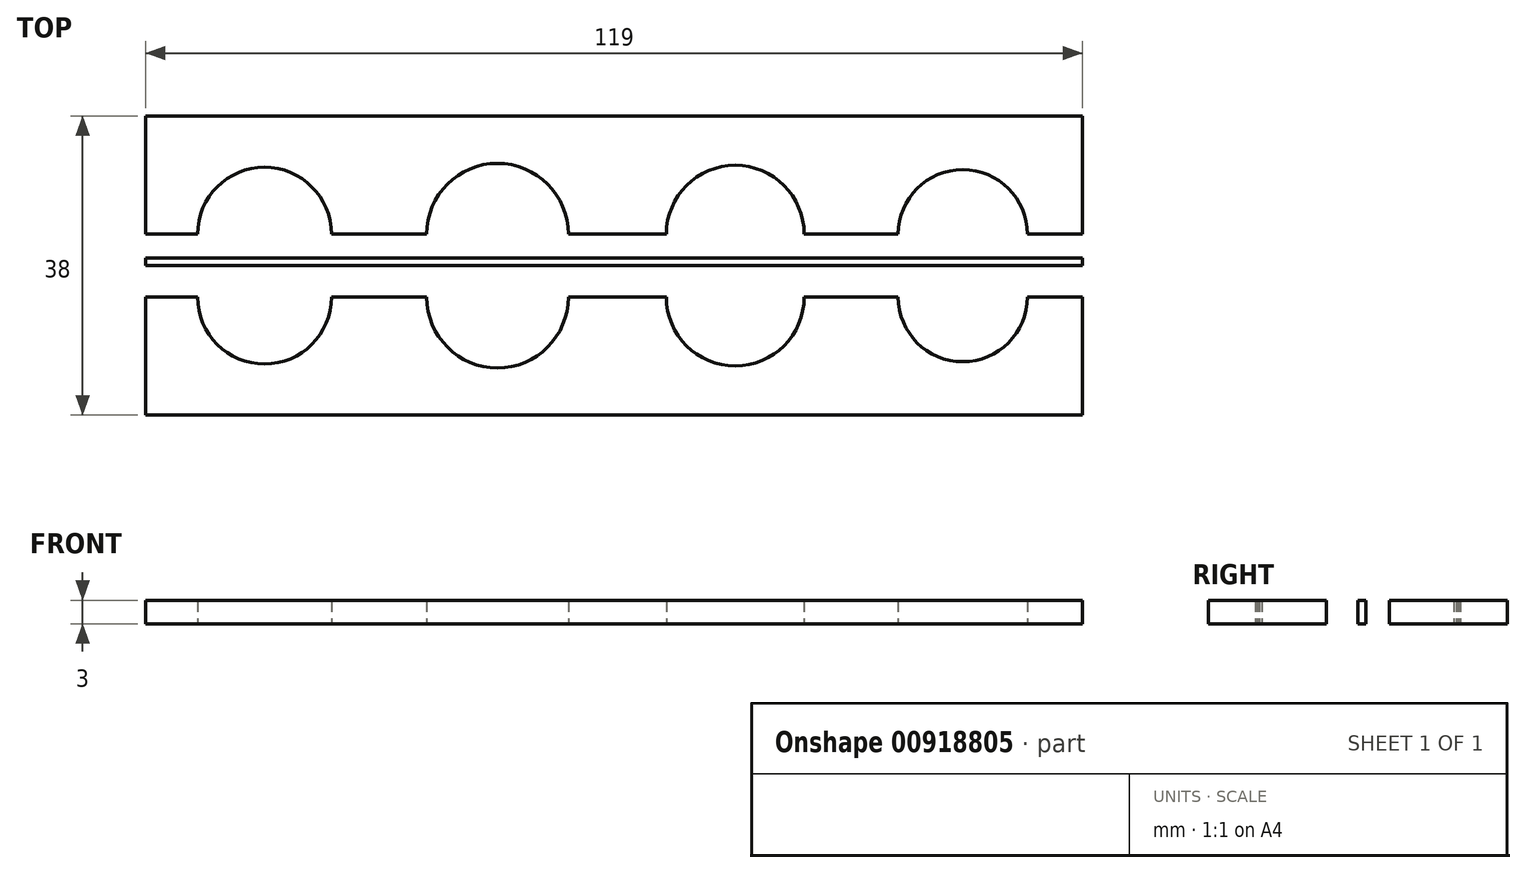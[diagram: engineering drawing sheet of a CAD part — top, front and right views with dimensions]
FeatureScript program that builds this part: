
annotation { "Feature Type Name" : "Feature", "Feature Type Description" : "" }
export const myFeature = defineFeature(function(context is Context, id is Id, definition is map)
    precondition{}
    {
        {
            var Q0;
            Q0=qCreatedBy(makeId("Top.planeOp"),FACE);
            var sketch = newSketch(context, id + "F0", { "sketchPlane" : qUnion([Q0])});
            skLineSegment(sketch, "E0.top", {"start": v(59.5, 15) * mm, "end": v(-59.5, 15) * mm});
            skLineSegment(sketch, "E0.left", {"start": v(59.5, 0) * mm, "end": v(59.5, 15) * mm});
            skLineSegment(sketch, "E0.right", {"start": v(-59.5, 0) * mm, "end": v(-59.5, 15) * mm});
            skPoint(sketch, "E0.middle", {"position": v(0, 0) * mm});
            skLineSegment(sketch, "E1", {"start": v(-59.5, 0) * mm, "end": v(-57.9, 0) * mm});
            skLineSegment(sketch, "E2", {"start": v(-57.9, 0) * mm, "end": v(-44.4, 0) * mm});
            skLineSegment(sketch, "E3", {"start": v(-44.4, 0) * mm, "end": v(-30.9, 0) * mm});
            skLineSegment(sketch, "E4", {"start": v(-30.9, 0) * mm, "end": v(-29.3, 0) * mm});
            skLineSegment(sketch, "E5", {"start": v(-29.3, 0) * mm, "end": v(-14.8, 0) * mm});
            skLineSegment(sketch, "E6", {"start": v(-14.8, 0) * mm, "end": v(-0.3, 0) * mm});
            skLineSegment(sketch, "E7", {"start": v(-0.3, 0) * mm, "end": v(1.3, 0) * mm});
            skLineSegment(sketch, "E8", {"start": v(1.3, 0) * mm, "end": v(15.4, 0) * mm});
            skLineSegment(sketch, "E9", {"start": v(15.4, 0) * mm, "end": v(29.5, 0) * mm});
            skLineSegment(sketch, "E10", {"start": v(29.5, 0) * mm, "end": v(31.1, 0) * mm});
            skLineSegment(sketch, "E11", {"start": v(31.1, 0) * mm, "end": v(44.3, 0) * mm});
            skLineSegment(sketch, "E12", {"start": v(44.3, 0) * mm, "end": v(57.5, 0) * mm});
            skLineSegment(sketch, "E13", {"start": v(57.5, 0) * mm, "end": v(59.5, 0) * mm});
            skArc(sketch, "E14", {"start": v(-35.9, 0) * mm, "mid": v(-44.4, 8.5) * mm, "end": v(-52.9, 0) * mm});
            skArc(sketch, "E15", {"start": v(-5.8, 0) * mm, "mid": v(-14.8, 9) * mm, "end": v(-23.8, 0) * mm});
            skArc(sketch, "E16", {"start": v(24.15, 0) * mm, "mid": v(15.4, 8.75) * mm, "end": v(6.65, 0) * mm});
            skArc(sketch, "E17", {"start": v(52.5, 0) * mm, "mid": v(44.3, 8.2) * mm, "end": v(36.1, 0) * mm});
            skPoint(sketch, "E0.bottom.end.orphan", {"position": v(-59.5, -15) * mm});
            skPoint(sketch, "E0.bottom.start.orphan", {"position": v(59.5, -15) * mm});
            skLineSegment(sketch, "E18", {"start": v(59.5, 0) * mm, "end": v(59.5, -3) * mm});
            skLineSegment(sketch, "E19", {"start": v(59.5, -3) * mm, "end": v(-57.9, -3) * mm});
            skLineSegment(sketch, "E20", {"start": v(-57.9, -3) * mm, "end": v(-59.5, -3) * mm});
            skLineSegment(sketch, "E21", {"start": v(-59.5, -3) * mm, "end": v(-59.5, 0) * mm});
            skLineSegment(sketch, "E22", {"start": v(-59.5, -3) * mm, "end": v(-59.5, -4) * mm});
            skLineSegment(sketch, "E23", {"start": v(-59.5, -4) * mm, "end": v(59.5, -4) * mm});
            skLineSegment(sketch, "E24", {"start": v(59.5, -4) * mm, "end": v(59.5, -3) * mm});
            skSolve(sketch);
        }
        {
            var Q0;
            Q0=makeQuery(id+"F0.imprint","IMPRINT",FACE,{"disambiguationData":[TD([[makeQuery(id+"F0.imprint","IMPRINT",EDGE,{"derivedFrom":sQuery(id+"F0.wireOp",EDGE,"E0.top")}),1.0]])]});
            var Q1;
            Q1=makeQuery(id+"F0.imprint","IMPRINT",FACE,{"disambiguationData":[TD([[makeQuery(id+"F0.imprint","IMPRINT",EDGE,{"derivedFrom":sQuery(id+"F0.wireOp",EDGE,"E19")}),1.0]])]});
            extrude(context, id + "F1", {"entities" : qUnion([Q0, Q1]), "depth" : 3 * mm, "offsetDistance" : 25 * mm});
        }
        {
            var Q0;
            Q0=makeQuery(id+"F1.opExtrude","SWEPT_BODY",BODY,{"disambiguationData":[OSD([sQuery(id+"F0.wireOp",EDGE,"E0.top"),sQuery(id+"F0.wireOp",EDGE,"E0.left"),sQuery(id+"F0.wireOp",EDGE,"E0.right"),sQuery(id+"F0.wireOp",EDGE,"E1"),sQuery(id+"F0.wireOp",EDGE,"E2"),sQuery(id+"F0.wireOp",EDGE,"E3"),sQuery(id+"F0.wireOp",EDGE,"E4"),sQuery(id+"F0.wireOp",EDGE,"E5"),sQuery(id+"F0.wireOp",EDGE,"E6"),sQuery(id+"F0.wireOp",EDGE,"E7"),sQuery(id+"F0.wireOp",EDGE,"E8"),sQuery(id+"F0.wireOp",EDGE,"E9"),sQuery(id+"F0.wireOp",EDGE,"E10"),sQuery(id+"F0.wireOp",EDGE,"E11"),sQuery(id+"F0.wireOp",EDGE,"E12"),sQuery(id+"F0.wireOp",EDGE,"E13"),sQuery(id+"F0.wireOp",EDGE,"E14"),sQuery(id+"F0.wireOp",EDGE,"E15"),sQuery(id+"F0.wireOp",EDGE,"E16"),sQuery(id+"F0.wireOp",EDGE,"E17")])]});
            var Q1;
            Q1=makeQuery(id+"F1.opExtrude","SWEPT_FACE",FACE,{"disambiguationData":[OSD([sQuery(id+"F0.wireOp",EDGE,"E23")])]});
            mirror(context, id + "F2", {"entities" : qUnion([Q0]), "mirrorPlane" : qUnion([Q1])});
        }
    });
